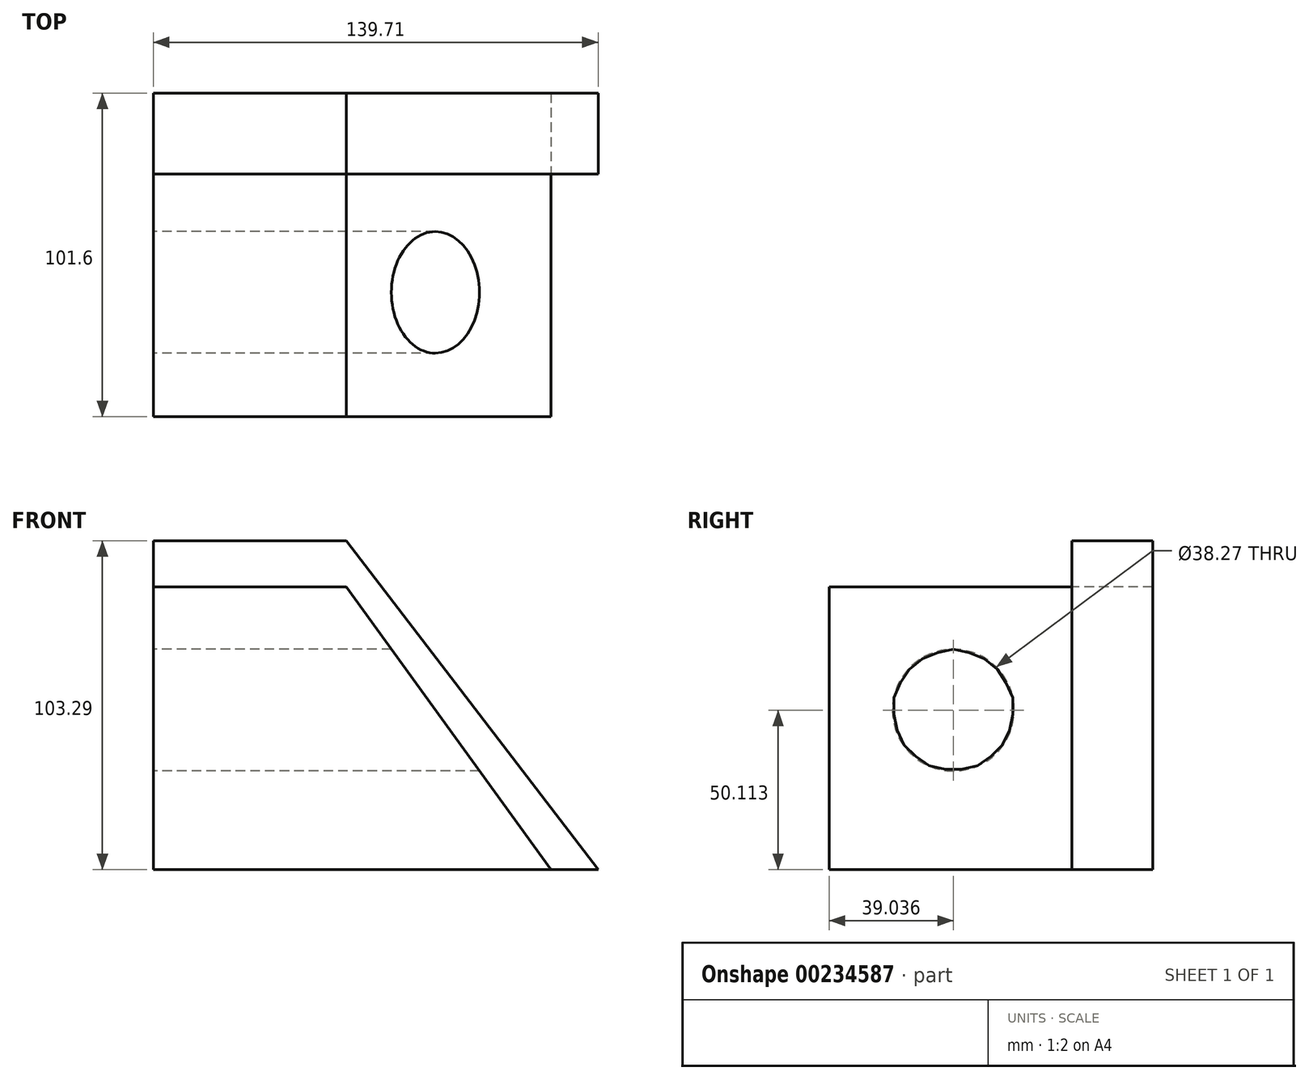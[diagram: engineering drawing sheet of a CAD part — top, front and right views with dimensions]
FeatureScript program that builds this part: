
annotation { "Feature Type Name" : "Feature", "Feature Type Description" : "" }
export const myFeature = defineFeature(function(context is Context, id is Id, definition is map)
    precondition{}
    {
        {
            var Q0;
            Q0=qCreatedBy(makeId("Front.planeOp"),FACE);
            var sketch = newSketch(context, id + "F0", { "sketchPlane" : qUnion([Q0])});
            skLineSegment(sketch, "E0.bottom", {"start": v(-52.05, -34.24) * mm, "end": v(8.54, -34.24) * mm});
            skLineSegment(sketch, "E0.top", {"start": v(-52.05, 54.55) * mm, "end": v(8.54, 54.55) * mm});
            skLineSegment(sketch, "E0.left", {"start": v(-52.05, -34.24) * mm, "end": v(-52.05, 54.55) * mm});
            skLineSegment(sketch, "E1", {"start": v(8.54, 54.55) * mm, "end": v(72.85, -34.24) * mm});
            skLineSegment(sketch, "E2", {"start": v(72.85, -34.24) * mm, "end": v(8.54, -34.24) * mm});
            skSolve(sketch);
        }
        {
            var Q0;
            Q0 = qSketchRegion(id + "F0", true);
            extrude(context, id + "F1", {"entities" : qUnion([Q0]), "depth" : 50.8 * mm, "hasSecondDirection" : true, "secondDirectionOppositeDirection" : true, "secondDirectionDepth" : 25.4 * mm});
        }
        {
            var Q0;
            Q0=makeQuery(id+"F1.opExtrude","CAP_FACE",FACE,{"disambiguationData":[OSD([sQuery(id+"F0.wireOp",EDGE,"E0.bottom"),sQuery(id+"F0.wireOp",EDGE,"E0.top"),sQuery(id+"F0.wireOp",EDGE,"E0.left"),sQuery(id+"F0.wireOp",EDGE,"E1"),sQuery(id+"F0.wireOp",EDGE,"E2")])],"isStart":true});
            var sketch = newSketch(context, id + "F2", { "sketchPlane" : qUnion([Q0])});
            skLineSegment(sketch, "E3.bottom", {"start": v(52.05, 54.55) * mm, "end": v(-8.54, 54.55) * mm});
            skLineSegment(sketch, "E3.top", {"start": v(52.05, 69.05) * mm, "end": v(-8.54, 69.05) * mm});
            skLineSegment(sketch, "E3.left", {"start": v(52.05, 54.55) * mm, "end": v(52.05, 69.05) * mm});
            skLineSegment(sketch, "E3.right", {"start": v(-8.54, 54.55) * mm, "end": v(-8.54, 69.05) * mm});
            skLineSegment(sketch, "E4", {"start": v(-8.54, 69.05) * mm, "end": v(-87.66, -34.24) * mm});
            skLineSegment(sketch, "E5", {"start": v(-87.66, -34.24) * mm, "end": v(-72.85, -34.24) * mm});
            skSolve(sketch);
        }
        {
            var Q0;
            Q0 = qSketchRegion(id + "F2", true);
            var Q1;
            Q1=makeQuery(id+"F2.imprint","IMPRINT",FACE,{"disambiguationData":[TD([[makeQuery(id+"F2.imprint","IMPRINT",EDGE,{"derivedFrom":sQuery(id+"F2.wireOp",EDGE,"E3.right")}),1.0]])]});
            extrude(context, id + "F3", {"entities" : qUnion([Q0, Q1]), "depth" : 25.4 * mm});
        }
        {
            var Q0;
            Q0=qCreatedBy(makeId("Right.planeOp"),FACE);
            var sketch = newSketch(context, id + "F4", { "sketchPlane" : qUnion([Q0])});
            skCircle(sketch, "E6", {"center": v(-11.76, 15.87) * mm, "radius": 19.13 * mm});
            skSolve(sketch);
        }
        {
            var Q0;
            Q0 = qSketchRegion(id + "F4", true);
            extrude(context, id + "F5", {"entities" : qUnion([Q0]), "operationType" : NewBodyOperationType.REMOVE, "depth" : 90.68 * mm, "hasSecondDirection" : true, "secondDirectionOppositeDirection" : true, "secondDirectionDepth" : 117.6 * mm});
        }
    });
